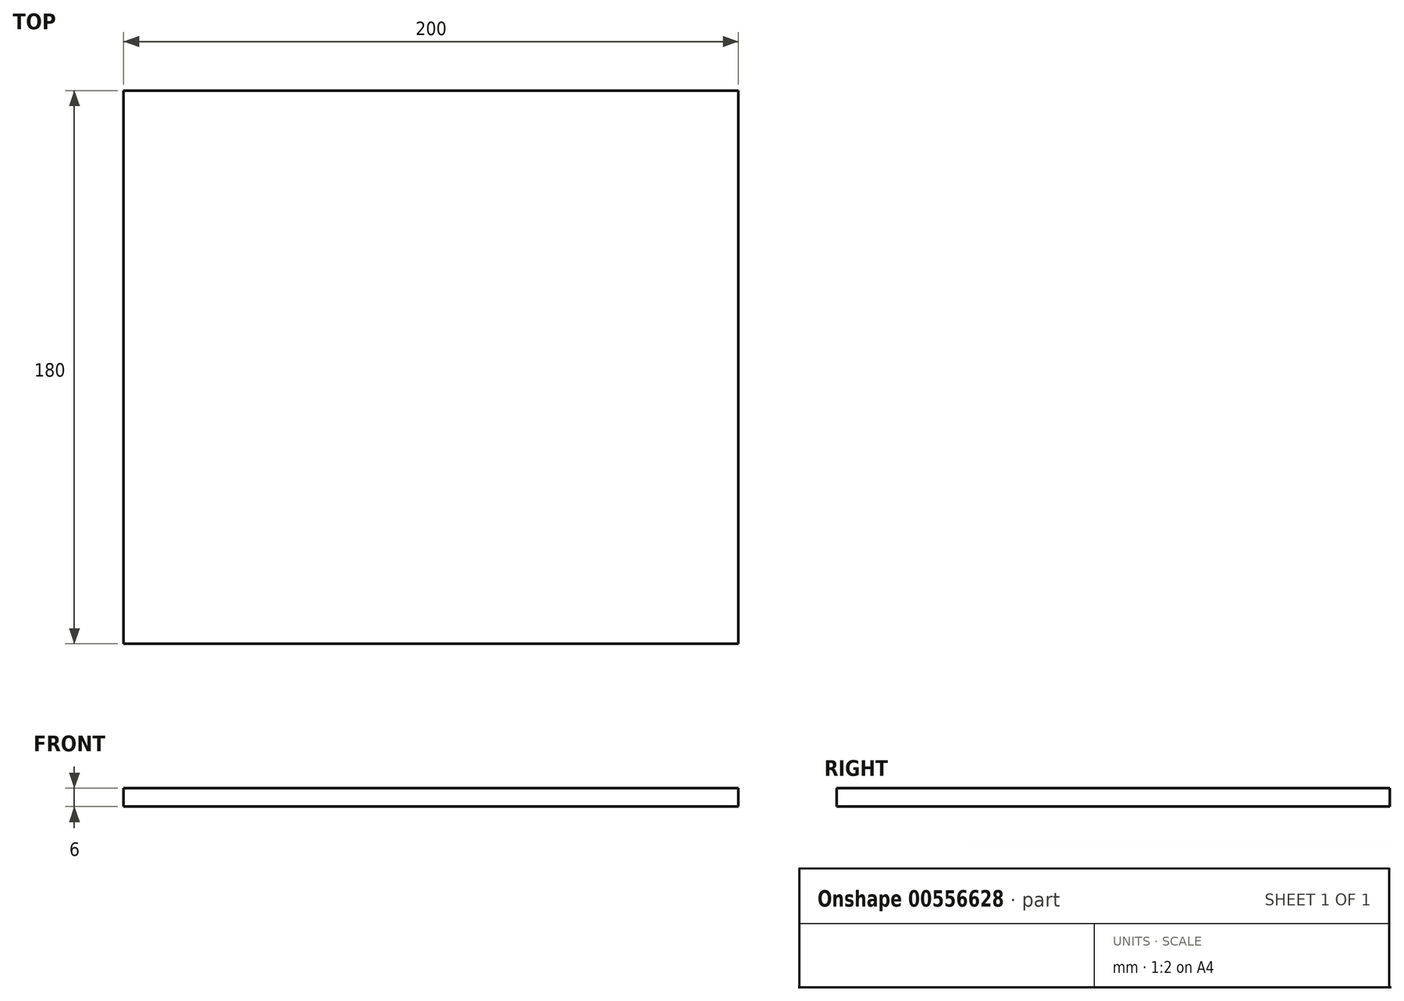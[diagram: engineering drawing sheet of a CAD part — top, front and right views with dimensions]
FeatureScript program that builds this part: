
annotation { "Feature Type Name" : "Feature", "Feature Type Description" : "" }
export const myFeature = defineFeature(function(context is Context, id is Id, definition is map)
    precondition{}
    {
        {
            var Q0;
            Q0=qCreatedBy(makeId("Top.planeOp"),FACE);
            var sketch = newSketch(context, id + "F0", { "sketchPlane" : qUnion([Q0])});
            skLineSegment(sketch, "E0", {"start": v(0, 0) * mm, "end": v(0, 180) * mm});
            skLineSegment(sketch, "E1", {"start": v(0, 180) * mm, "end": v(200, 180) * mm});
            skLineSegment(sketch, "E2", {"start": v(200, 180) * mm, "end": v(200, 0) * mm});
            skLineSegment(sketch, "E3", {"start": v(200, 0) * mm, "end": v(0, 0) * mm});
            skSolve(sketch);
        }
        {
            var Q0;
            Q0=makeQuery(id+"F0.imprint","IMPRINT",FACE,{"disambiguationData":[TD([[makeQuery(id+"F0.imprint","IMPRINT",EDGE,{"derivedFrom":sQuery(id+"F0.wireOp",EDGE,"E0")}),-1.0]])]});
            extrude(context, id + "F1", {"entities" : qUnion([Q0]), "depth" : 6 * mm, "offsetDistance" : 25 * mm});
        }
    });
